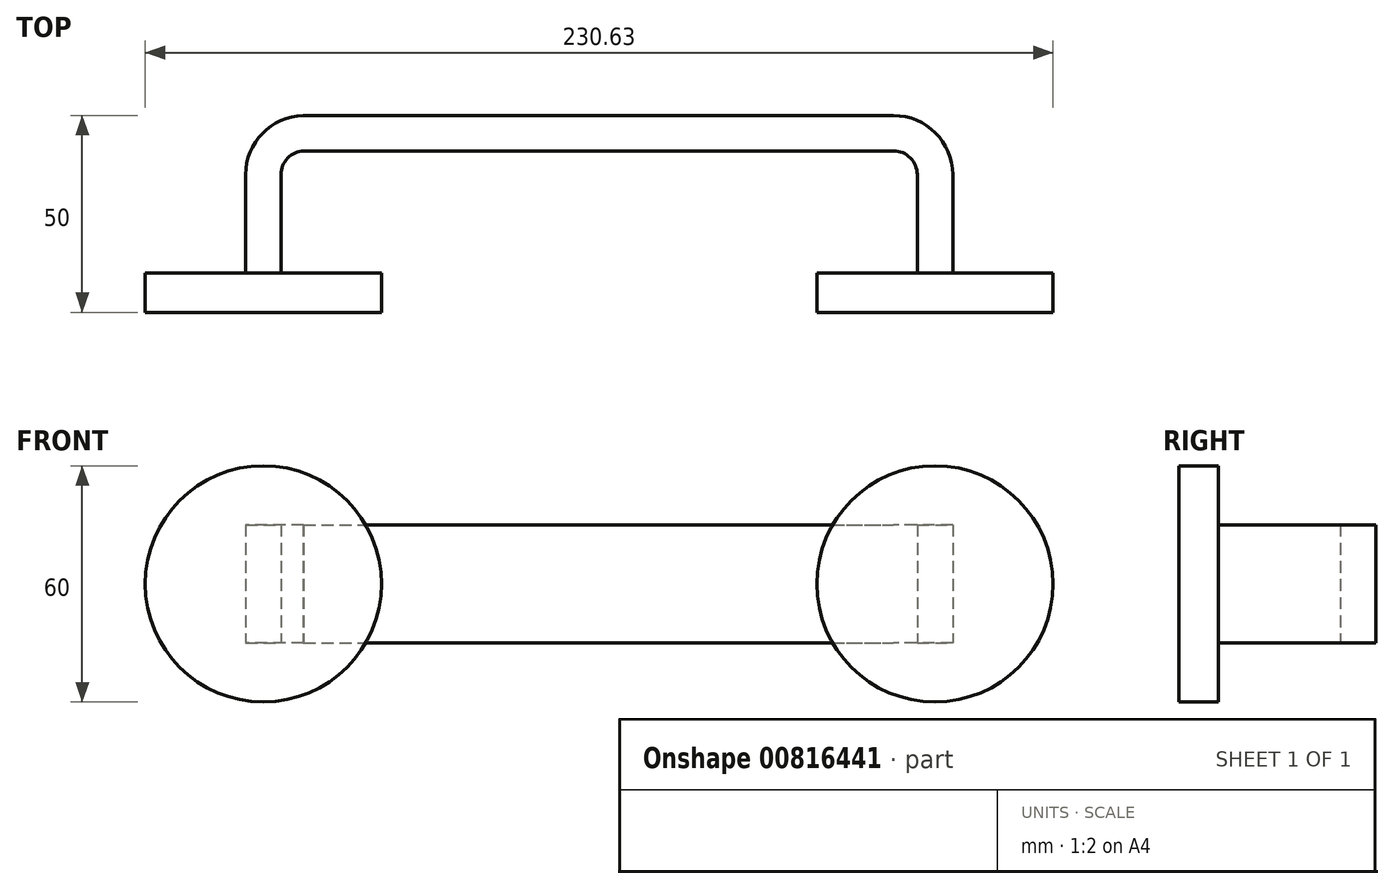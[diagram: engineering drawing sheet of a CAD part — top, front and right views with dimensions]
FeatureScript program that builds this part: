
annotation { "Feature Type Name" : "Feature", "Feature Type Description" : "" }
export const myFeature = defineFeature(function(context is Context, id is Id, definition is map)
    precondition{}
    {
        {
            var Q0;
            Q0=qCreatedBy(makeId("Top.planeOp"),FACE);
            var sketch = newSketch(context, id + "F0", { "sketchPlane" : qUnion([Q0])});
            skLineSegment(sketch, "E0", {"start": v(-83.63, -25) * mm, "end": v(-83.63, 0) * mm});
            skLineSegment(sketch, "E1", {"start": v(-69, 15) * mm, "end": v(81, 15) * mm});
            skLineSegment(sketch, "E2", {"start": v(96, 0) * mm, "end": v(96, -25) * mm});
            skArc(sketch, "E3", {"start": v(-83.63, 0) * mm, "mid": v(-79.37, 10.47) * mm, "end": v(-69, 15) * mm});
            skArc(sketch, "E4", {"start": v(81, 15) * mm, "mid": v(91.6, 10.6) * mm, "end": v(96, 0) * mm});
            skLineSegment(sketch, "E5.0", {"start": v(87, 0) * mm, "end": v(87, -25) * mm});
            skLineSegment(sketch, "E5.1", {"start": v(-74.63, -25) * mm, "end": v(-74.63, 0) * mm});
            skArc(sketch, "E5.2", {"start": v(-74.63, 0) * mm, "mid": v(-72.96, 4.16) * mm, "end": v(-68.87, 6) * mm});
            skLineSegment(sketch, "E5.3", {"start": v(-68.87, 6) * mm, "end": v(81, 6) * mm});
            skArc(sketch, "E5.4", {"start": v(81, 6) * mm, "mid": v(85.24, 4.24) * mm, "end": v(87, 0) * mm});
            skLineSegment(sketch, "E6", {"start": v(-83.63, -25) * mm, "end": v(-74.63, -25) * mm});
            skLineSegment(sketch, "E7", {"start": v(87, -25) * mm, "end": v(96, -25) * mm});
            skSolve(sketch);
        }
        {
            var Q0;
            Q0 = qSketchRegion(id + "F0", true);
            extrude(context, id + "F1", {"entities" : qUnion([Q0]), "depth" : 30 * mm, "offsetDistance" : 25 * mm});
        }
        {
            var Q0;
            Q0=makeQuery(id+"F1.opExtrude","SWEPT_FACE",FACE,{"disambiguationData":[OSD([sQuery(id+"F0.wireOp",EDGE,"E6")])]});
            var sketch = newSketch(context, id + "F2", { "sketchPlane" : qUnion([Q0])});
            skLineSegment(sketch, "E8", {"start": v(-79.13, 30) * mm, "end": v(-79.13, 0) * mm, "construction": true});
            skLineSegment(sketch, "E9", {"start": v(-74.63, 15) * mm, "end": v(-83.63, 15) * mm, "construction": true});
            skCircle(sketch, "E10", {"center": v(-79.13, 15) * mm, "radius": 30 * mm});
            skSolve(sketch);
        }
        {
            var Q0;
            Q0 = qSketchRegion(id + "F2", true);
            extrude(context, id + "F3", {"entities" : qUnion([Q0]), "operationType" : NewBodyOperationType.ADD, "depth" : 10 * mm, "offsetDistance" : 25 * mm});
        }
        {
            var Q0;
            Q0=makeQuery(id+"F1.opExtrude","SWEPT_FACE",FACE,{"disambiguationData":[OSD([sQuery(id+"F0.wireOp",EDGE,"E7")])]});
            var sketch = newSketch(context, id + "F4", { "sketchPlane" : qUnion([Q0])});
            skLineSegment(sketch, "E11", {"start": v(91.5, 30) * mm, "end": v(91.5, 0) * mm, "construction": true});
            skLineSegment(sketch, "E12", {"start": v(96, 15) * mm, "end": v(87, 15) * mm, "construction": true});
            skPoint(sketch, "E13", {"position": v(91.5, 15) * mm});
            skCircle(sketch, "E14", {"center": v(91.5, 15) * mm, "radius": 30 * mm});
            skSolve(sketch);
        }
        {
            var Q0;
            Q0 = qSketchRegion(id + "F4", true);
            extrude(context, id + "F5", {"entities" : qUnion([Q0]), "operationType" : NewBodyOperationType.ADD, "depth" : 10 * mm, "offsetDistance" : 25 * mm});
        }
    });
